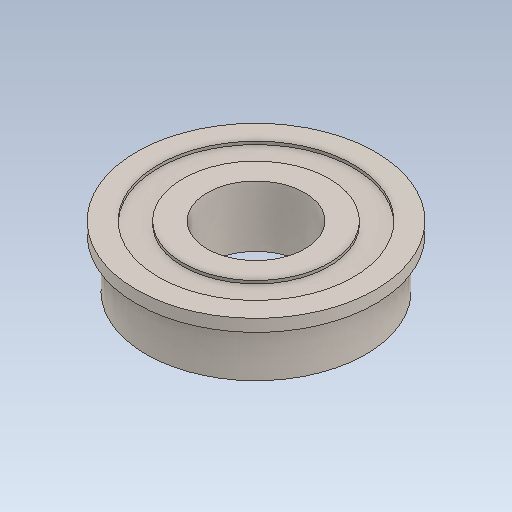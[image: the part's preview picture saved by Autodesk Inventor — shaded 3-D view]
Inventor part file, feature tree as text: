
AUTODESK INVENTOR PART (.ipt)
format: ipt  version: 2020 (Build 240168000, 168)  size: 126,976 bytes
history: native  units: in
note: dims shown in document units (in); Inventor stores cm internally (conversion verified against a paired STEP export)
features: revolve x1
ambient origin geometry x8: Origin, YZ Plane, XZ Plane, XY Plane, X Axis, Y Axis, Z Axis, Center Point
bodies: Solid1 (feature_tree)
feature tree (1):
  revolve  "Revolve1"  [1 undecoded]
note: 1 required parameter value undecoded (feature->parameter linkage not recoverable at this tier; creation-order binding heuristic only, values carry confidence <= 0.55)
